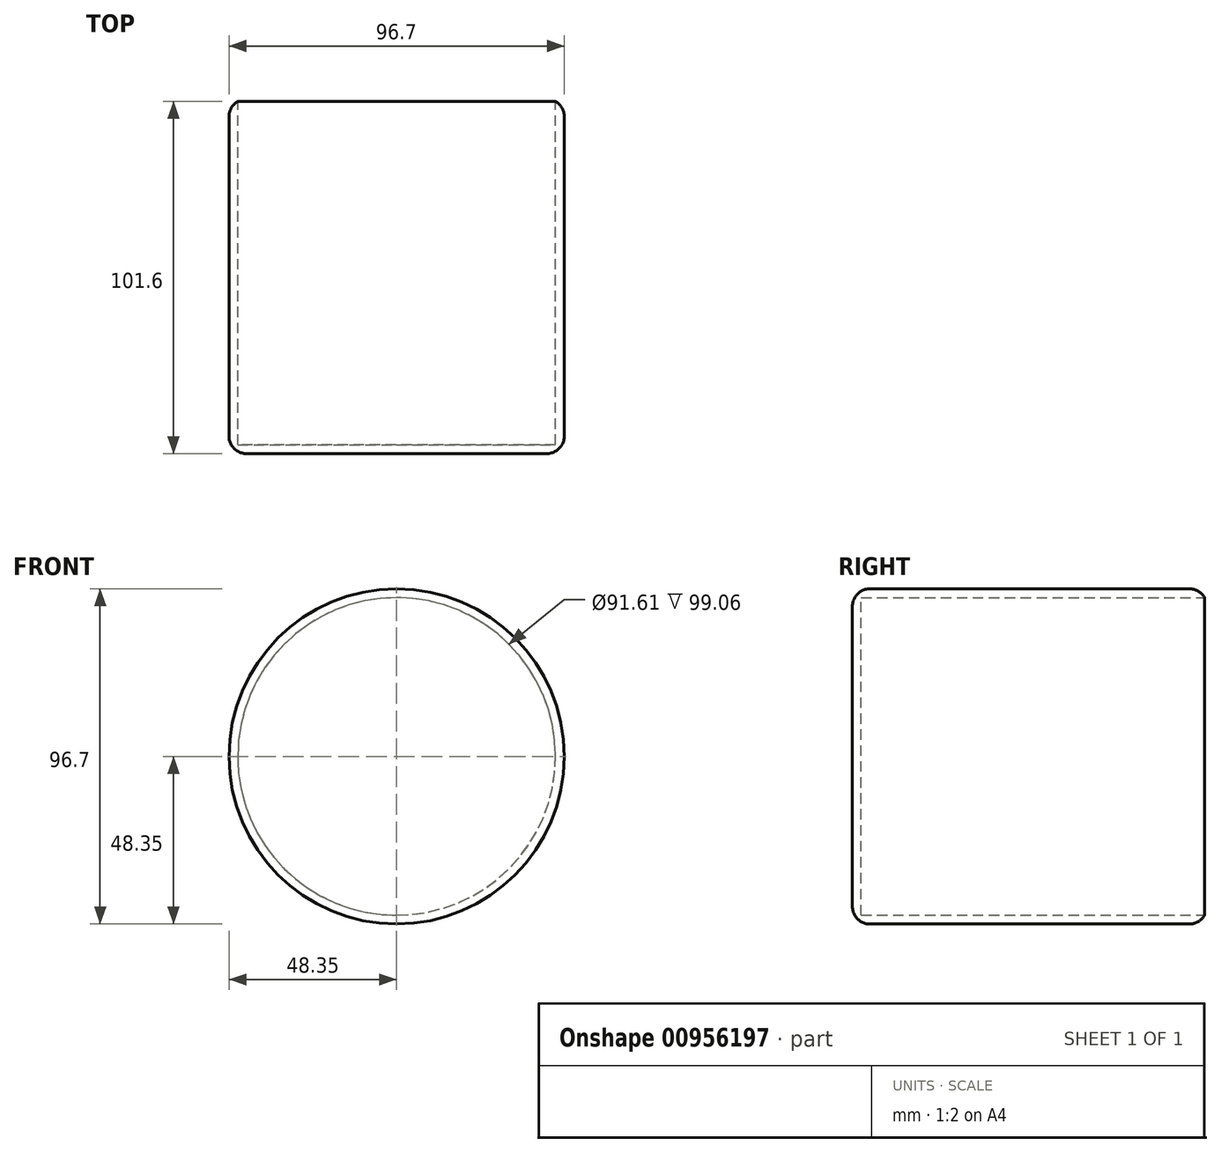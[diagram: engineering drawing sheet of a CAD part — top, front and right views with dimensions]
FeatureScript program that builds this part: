
annotation { "Feature Type Name" : "Feature", "Feature Type Description" : "" }
export const myFeature = defineFeature(function(context is Context, id is Id, definition is map)
    precondition{}
    {
        {
            var Q0;
            Q0=qCreatedBy(makeId("Front.planeOp"),FACE);
            var sketch = newSketch(context, id + "F0", { "sketchPlane" : qUnion([Q0])});
            skCircle(sketch, "E0", {"center": v(0, 0) * mm, "radius": 48.35 * mm});
            skSolve(sketch);
        }
        {
            var Q0;
            Q0=makeQuery(id+"F0.imprint","IMPRINT",FACE,{"disambiguationData":[TD([[makeQuery(id+"F0.imprint","IMPRINT",EDGE,{"derivedFrom":sQuery(id+"F0.wireOp",EDGE,"E0")}),1.0]])]});
            extrude(context, id + "F1", {"entities" : qUnion([Q0]), "endBound" : BoundingType.SYMMETRIC, "depth" : 101.6 * mm, "offsetDistance" : 25.4 * mm});
        }
        {
            var Q0;
            Q0=makeQuery(id+"F1.opExtrude","CAP_FACE",FACE,{"disambiguationData":[OSD([sQuery(id+"F0.wireOp",EDGE,"E0")])],"isStart":true});
            shell(context, id + "F2", {"entities" : qUnion([Q0]), "thickness" : 2.54 * mm});
        }
        {
            var Q0;
            Q0=makeQuery(id+"F1.opExtrude","SWEPT_FACE",FACE,{"disambiguationData":[OSD([sQuery(id+"F0.wireOp",EDGE,"E0")])]});
            fillet(context, id + "F3", {"entities" : qUnion([Q0]), "radius" : 5.08 * mm, "tangentPropagation" : true, "allowEdgeOverflow" : false});
        }
    });
